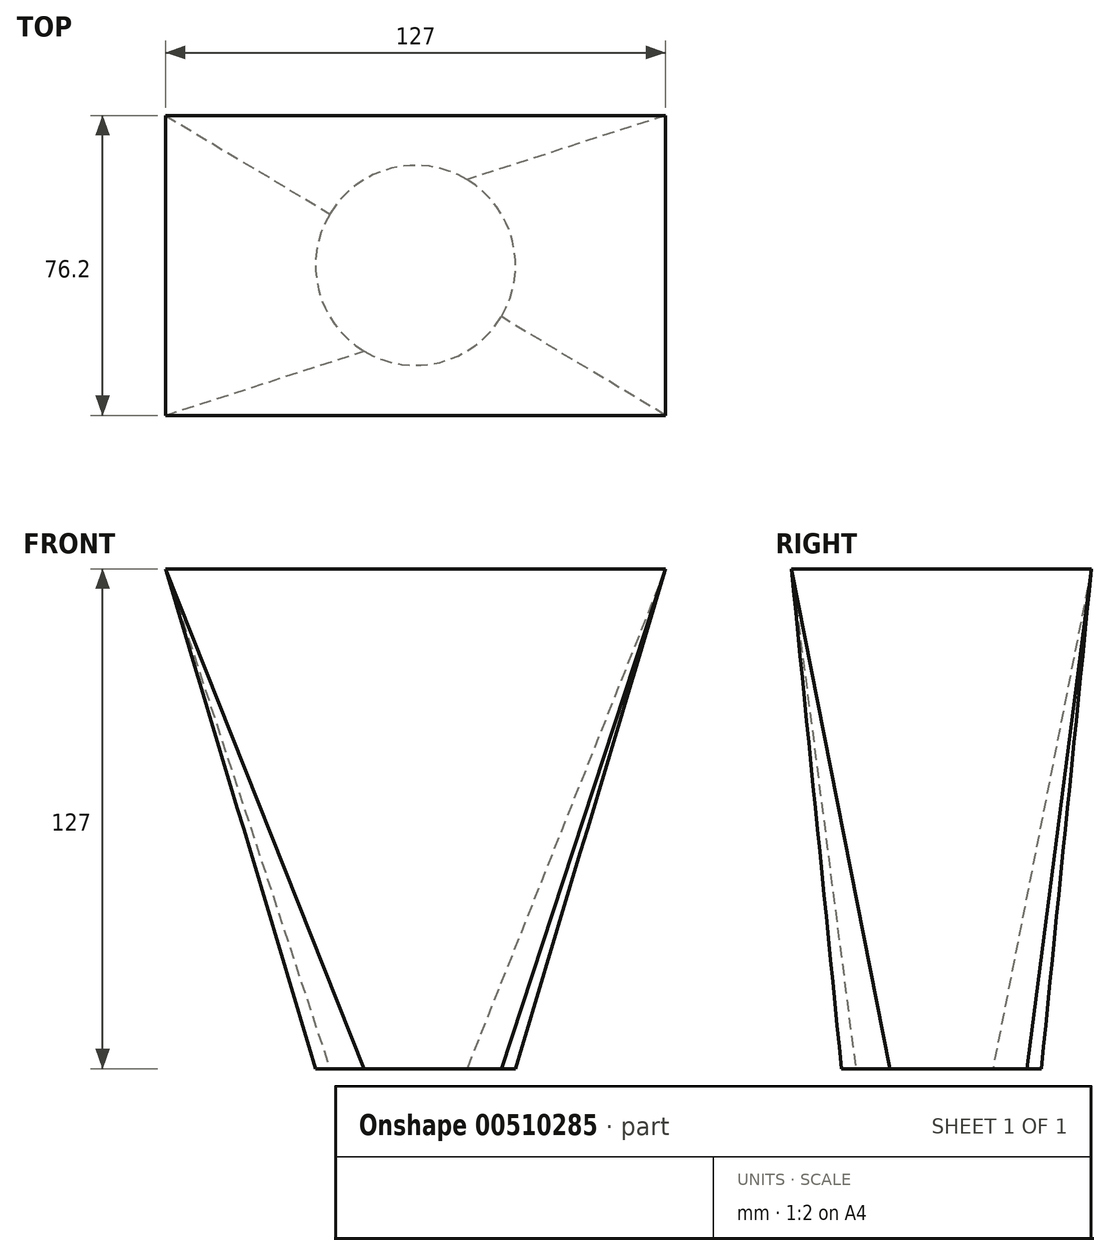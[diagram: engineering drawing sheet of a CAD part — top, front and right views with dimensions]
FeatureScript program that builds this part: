
annotation { "Feature Type Name" : "Feature", "Feature Type Description" : "" }
export const myFeature = defineFeature(function(context is Context, id is Id, definition is map)
    precondition{}
    {
        {
            var Q0;
            Q0=qCreatedBy(makeId("Top.planeOp"),FACE);
            var sketch = newSketch(context, id + "F0", { "sketchPlane" : qUnion([Q0])});
            skCircle(sketch, "E0", {"center": v(0, 0) * mm, "radius": 25.4 * mm});
            skSolve(sketch);
        }
        {
            var Q0;
            Q0=qCreatedBy(makeId("Top.planeOp"),FACE);
            cPlane(context, id + "F1", {"entities" : qUnion([Q0]), "cplaneType" : CPlaneType.OFFSET, "offset" : 127 * mm, "width" : 152.4 * mm, "height" : 152.4 * mm});
        }
        {
            var Q0;
            Q0=qCreatedBy(id+"F1.planeOp",FACE);
            var sketch = newSketch(context, id + "F2", { "sketchPlane" : qUnion([Q0])});
            skLineSegment(sketch, "E1.bottom", {"start": v(63.5, -38.1) * mm, "end": v(-63.5, -38.1) * mm});
            skLineSegment(sketch, "E1.top", {"start": v(63.5, 38.1) * mm, "end": v(-63.5, 38.1) * mm});
            skLineSegment(sketch, "E1.left", {"start": v(63.5, -38.1) * mm, "end": v(63.5, 38.1) * mm});
            skLineSegment(sketch, "E1.right", {"start": v(-63.5, -38.1) * mm, "end": v(-63.5, 38.1) * mm});
            skPoint(sketch, "E1.middle", {"position": v(0, 0) * mm});
            skSolve(sketch);
        }
        {
            var Q0;
            Q0=makeQuery(id+"F2.imprint","IMPRINT",FACE,{"disambiguationData":[TD([[makeQuery(id+"F2.imprint","IMPRINT",EDGE,{"derivedFrom":sQuery(id+"F2.wireOp",EDGE,"E1.bottom")}),-1.0]])]});
            var Q1;
            Q1=makeQuery(id+"F0.imprint","IMPRINT",FACE,{"disambiguationData":[TD([[makeQuery(id+"F0.imprint","IMPRINT",EDGE,{"derivedFrom":sQuery(id+"F0.wireOp",EDGE,"E0")}),1.0]])]});
            loft(context, id + "F3", {"sheetProfilesArray" : [{ "sheetProfileEntities" : qUnion([Q0]) }, { "sheetProfileEntities" : qUnion([Q1]) }]});
        }
    });
